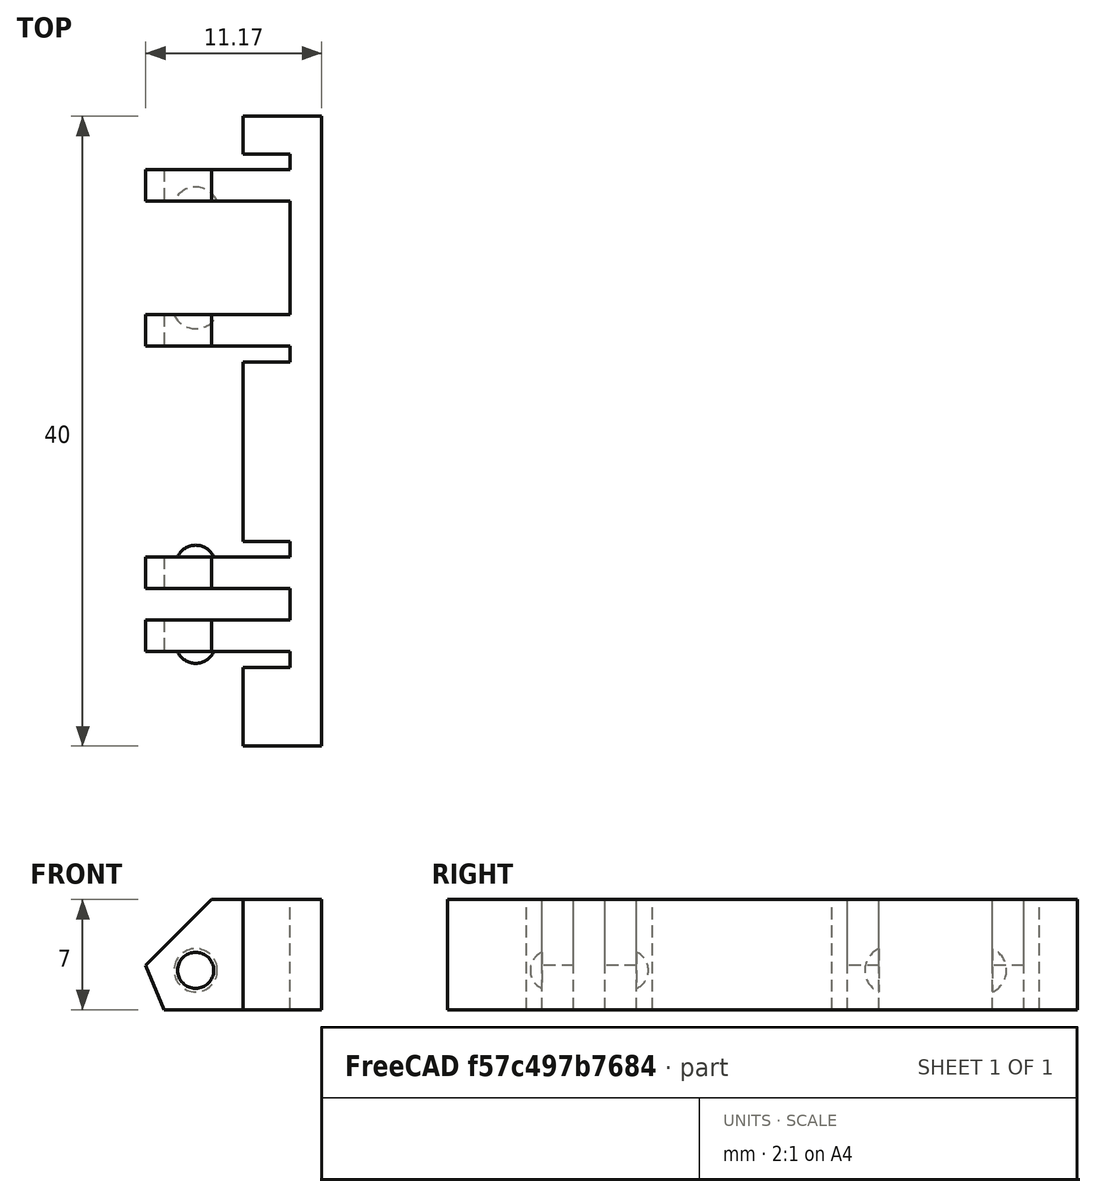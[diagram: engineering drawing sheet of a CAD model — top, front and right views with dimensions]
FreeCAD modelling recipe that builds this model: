
FCSTD DOCUMENT  (FreeCAD 0.17R13522 (Git))
Label: Bumps and dips edges
License: All rights reserved
LicenseURL: http://en.wikipedia.org/wiki/All_rights_reserved
objects: Part::Box×12, Part::Sphere×4, Part::MultiFuse×4, Part::Cut×3, Part::Chamfer×1
note: 24 computed .brp shape members not serialized (recipe doc carries the construction recipe); baked Part::Feature solids carry a one-line shape summary decoded from their .brp

FEATURE [Part::Box] Box  label="Cube"
  AttacherType = Attacher::AttachEngine3D
  Height = 7
  Length = 10
  Placement = pos=(-10,6,0) rot=(0,0,1;0rad)
  Width = 2
FEATURE [Part::Box] Box001  label="Cube001"
  AttacherType = Attacher::AttachEngine3D
  Height = 7
  Length = 5
  Width = 40
FEATURE [Part::Box] Box002  label="Cube002"
  AttacherType = Attacher::AttachEngine3D
  Height = 7
  Length = 10
  Placement = pos=(-10,10,0) rot=(0,0,1;0rad)
  Width = 2
FEATURE [Part::Box] Box003  label="Cube003"
  AttacherType = Attacher::AttachEngine3D
  Height = 7
  Length = 10
  Placement = pos=(-10,25.4,0) rot=(0,0,1;0rad)
  Width = 2
FEATURE [Part::Box] Box004  label="Cube004"
  AttacherType = Attacher::AttachEngine3D
  Height = 7
  Length = 10
  Placement = pos=(-10,34.6,0) rot=(0,0,1;0rad)
  Width = 2
FEATURE [Part::Sphere] Sphere008
  Angle1 = -90
  Angle2 = 90
  Angle3 = 360
  AttacherType = Attacher::AttachEngine3D
  Placement = pos=(-3,6.5,2.5) rot=(0,0,1;0rad)
  Radius = 1.25
FEATURE [Part::Box] Box005  label="Cube005"
  AttacherType = Attacher::AttachEngine3D
  Height = 10
  Length = 13
  Placement = pos=(-10.19,0,-1.19) rot=(0,-1,0;0.785398rad)
  Width = 40
FEATURE [Part::Sphere] Sphere009
  Angle1 = -90
  Angle2 = 90
  Angle3 = 360
  AttacherType = Attacher::AttachEngine3D
  Placement = pos=(-3,11.5,2.5) rot=(0,0,1;0rad)
  Radius = 1.25
FEATURE [Part::Sphere] Sphere010
  Angle1 = -90
  Angle2 = 90
  Angle3 = 360
  AttacherType = Attacher::AttachEngine3D
  Placement = pos=(-3,28,2.5) rot=(0,0,1;0rad)
  Radius = 1.5
FEATURE [Part::Sphere] Sphere011
  Angle1 = -90
  Angle2 = 90
  Angle3 = 360
  AttacherType = Attacher::AttachEngine3D
  Placement = pos=(-3,34,2.5) rot=(0,0,1;0rad)
  Radius = 1.5
FEATURE [Part::MultiFuse] Fusion
  Shapes = -> [Box001,Box,Box002,Box003,Box004]
FEATURE [Part::Cut] Cut
  Base = -> Fusion
  Tool = -> Box005
FEATURE [Part::MultiFuse] Fusion001
  Shapes = -> [Sphere008,Sphere009,Cut]
FEATURE [Part::MultiFuse] Fusion002
  Shapes = -> [Sphere011,Sphere010]
FEATURE [Part::Cut] Cut001
  Base = -> Fusion001
  Tool = -> Fusion002
FEATURE [Part::Chamfer] Chamfer
  Base = -> Cut001
  Edges = 4 edges r=4: [Edge31,Edge37,Edge43,Edge46]
FEATURE [Part::Box] Box006  label="Cube006"
  AttacherType = Attacher::AttachEngine3D
  Height = 7
  Length = 4
  Placement = pos=(-1,5,0) rot=(0,0,1;0rad)
  Width = 1
FEATURE [Part::Box] Box007  label="Cube007"
  AttacherType = Attacher::AttachEngine3D
  Height = 7
  Length = 4
  Placement = pos=(-1,8,0) rot=(0,0,1;0rad)
  Width = 2
FEATURE [Part::Box] Box008  label="Cube008"
  AttacherType = Attacher::AttachEngine3D
  Height = 7
  Length = 4
  Placement = pos=(-1,12,0) rot=(0,0,1;0rad)
  Width = 1
FEATURE [Part::Box] Box009  label="Cube009"
  AttacherType = Attacher::AttachEngine3D
  Height = 7
  Length = 4
  Placement = pos=(-1,24.4,0) rot=(0,0,1;0rad)
  Width = 1
FEATURE [Part::Box] Box010  label="Cube010"
  AttacherType = Attacher::AttachEngine3D
  Height = 7
  Length = 4
  Placement = pos=(-1,36.6,0) rot=(0,0,1;0rad)
  Width = 1
FEATURE [Part::Box] Box011  label="Cube011"
  AttacherType = Attacher::AttachEngine3D
  Height = 7
  Length = 4
  Placement = pos=(-1,27.4,0) rot=(0,0,1;0rad)
  Width = 7.2
FEATURE [Part::MultiFuse] Fusion003
  Shapes = -> [Box011,Box008,Box010,Box007,Box009,Box006]
FEATURE [Part::Cut] Cut002
  Base = -> Chamfer
  Tool = -> Fusion003
